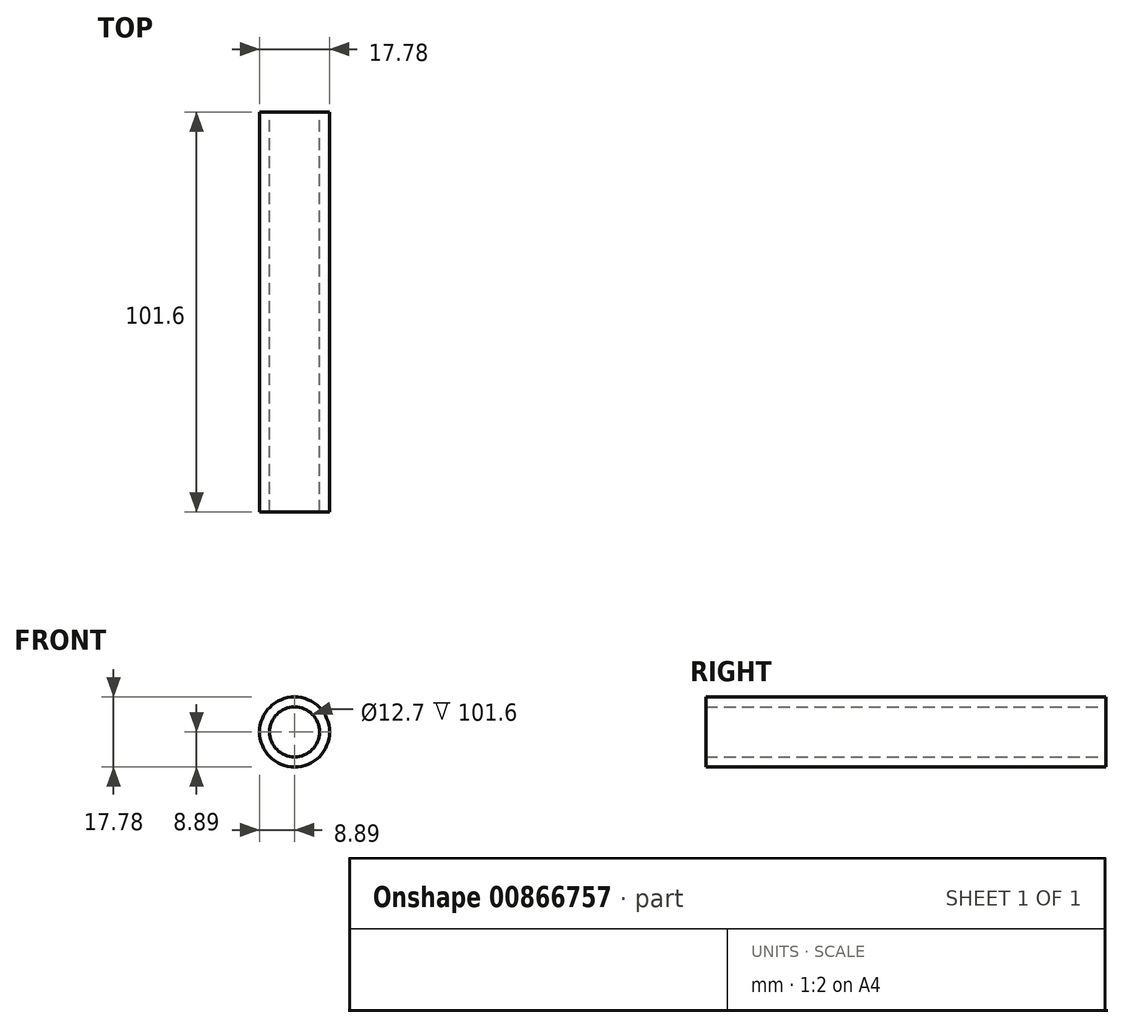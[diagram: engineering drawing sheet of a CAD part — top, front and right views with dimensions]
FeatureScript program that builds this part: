
annotation { "Feature Type Name" : "Feature", "Feature Type Description" : "" }
export const myFeature = defineFeature(function(context is Context, id is Id, definition is map)
    precondition{}
    {
        {
            var Q0;
            Q0=qCreatedBy(makeId("Front.planeOp"),FACE);
            var sketch = newSketch(context, id + "F0", { "sketchPlane" : qUnion([Q0])});
            skCircle(sketch, "E0", {"center": v(0, 0) * mm, "radius": 8.9 * mm});
            skCircle(sketch, "E1", {"center": v(0, 0) * mm, "radius": 6.35 * mm});
            skSolve(sketch);
        }
        {
            var Q0;
            Q0 = qSketchRegion(id + "F0", true);
            extrude(context, id + "F1", {"entities" : qUnion([Q0]), "endBound" : BoundingType.SYMMETRIC, "depth" : 101.6 * mm, "offsetDistance" : 25.4 * mm});
        }
    });
